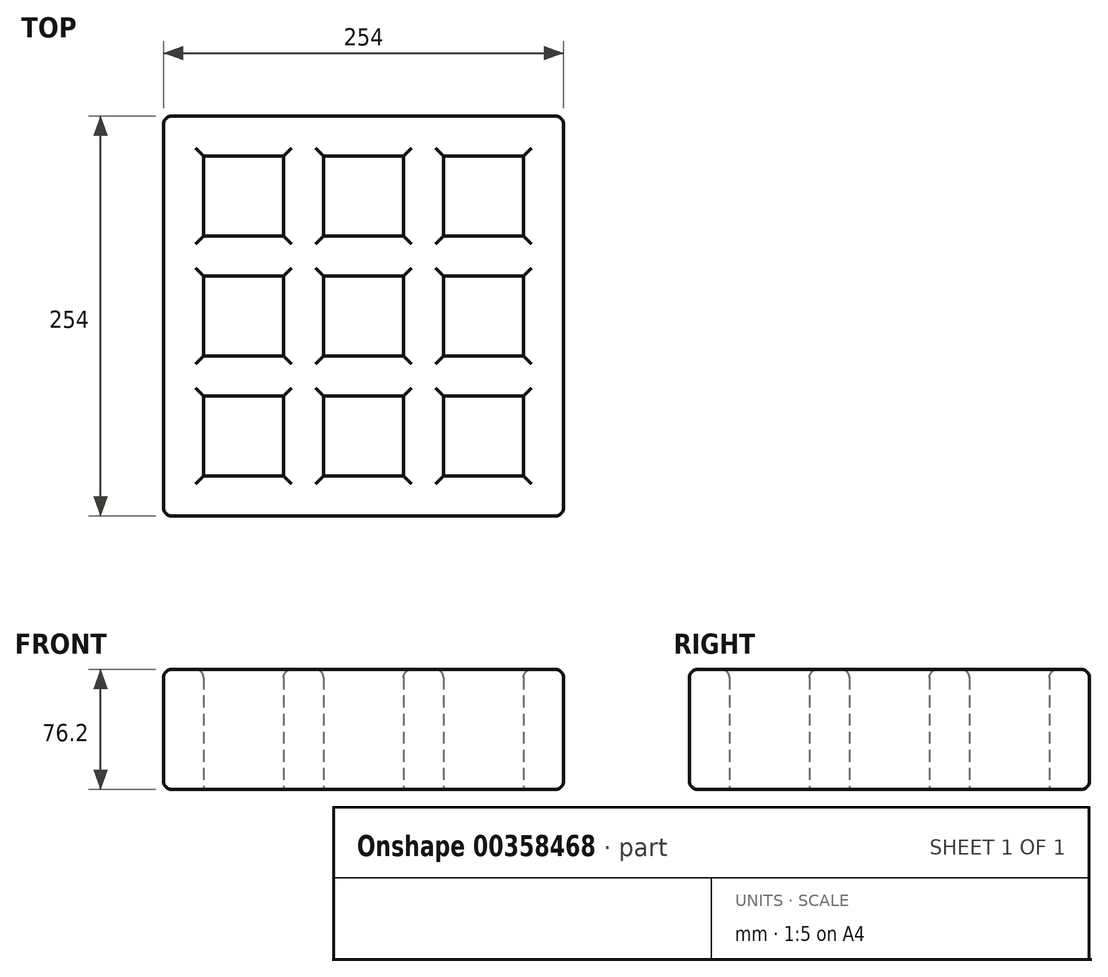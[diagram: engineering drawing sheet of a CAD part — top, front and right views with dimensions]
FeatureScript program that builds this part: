
annotation { "Feature Type Name" : "Feature", "Feature Type Description" : "" }
export const myFeature = defineFeature(function(context is Context, id is Id, definition is map)
    precondition{}
    {
        {
            var Q0;
            Q0=qCreatedBy(makeId("Top.planeOp"),FACE);
            var sketch = newSketch(context, id + "F0", { "sketchPlane" : qUnion([Q0])});
            skLineSegment(sketch, "E0.bottom", {"start": v(-126.07, 146.76) * mm, "end": v(127.93, 146.76) * mm});
            skLineSegment(sketch, "E0.top", {"start": v(-126.07, -107.24) * mm, "end": v(127.93, -107.24) * mm});
            skLineSegment(sketch, "E0.left", {"start": v(-126.07, 146.76) * mm, "end": v(-126.07, -107.24) * mm});
            skLineSegment(sketch, "E0.right", {"start": v(127.93, 146.76) * mm, "end": v(127.93, -107.24) * mm});
            skLineSegment(sketch, "E1.bottom", {"start": v(-100.67, 121.36) * mm, "end": v(-49.87, 121.36) * mm});
            skLineSegment(sketch, "E1.top", {"start": v(-100.67, 70.56) * mm, "end": v(-49.87, 70.56) * mm});
            skLineSegment(sketch, "E1.left", {"start": v(-100.67, 121.36) * mm, "end": v(-100.67, 70.56) * mm});
            skLineSegment(sketch, "E1.right", {"start": v(-49.87, 121.36) * mm, "end": v(-49.87, 70.56) * mm});
            skLineSegment(sketch, "E2.0.1.0", {"start": v(-49.87, 45.16) * mm, "end": v(-49.87, -5.64) * mm});
            skLineSegment(sketch, "E2.0.1.1", {"start": v(-100.67, 45.16) * mm, "end": v(-100.67, -5.64) * mm});
            skLineSegment(sketch, "E2.0.1.2", {"start": v(-100.67, -5.64) * mm, "end": v(-49.87, -5.64) * mm});
            skLineSegment(sketch, "E2.0.1.3", {"start": v(-100.67, 45.16) * mm, "end": v(-49.87, 45.16) * mm});
            skLineSegment(sketch, "E2.0.2.0", {"start": v(-49.87, -31.04) * mm, "end": v(-49.87, -81.84) * mm});
            skLineSegment(sketch, "E2.0.2.1", {"start": v(-100.67, -31.04) * mm, "end": v(-100.67, -81.84) * mm});
            skLineSegment(sketch, "E2.0.2.2", {"start": v(-100.67, -81.84) * mm, "end": v(-49.87, -81.84) * mm});
            skLineSegment(sketch, "E2.0.2.3", {"start": v(-100.67, -31.04) * mm, "end": v(-49.87, -31.04) * mm});
            skLineSegment(sketch, "E2.1.0.0", {"start": v(26.33, 121.36) * mm, "end": v(26.33, 70.56) * mm});
            skLineSegment(sketch, "E2.1.0.1", {"start": v(-24.47, 121.36) * mm, "end": v(-24.47, 70.56) * mm});
            skLineSegment(sketch, "E2.1.0.2", {"start": v(-24.47, 70.56) * mm, "end": v(26.33, 70.56) * mm});
            skLineSegment(sketch, "E2.1.0.3", {"start": v(-24.47, 121.36) * mm, "end": v(26.33, 121.36) * mm});
            skLineSegment(sketch, "E2.1.1.0", {"start": v(26.33, 45.16) * mm, "end": v(26.33, -5.64) * mm});
            skLineSegment(sketch, "E2.1.1.1", {"start": v(-24.47, 45.16) * mm, "end": v(-24.47, -5.64) * mm});
            skLineSegment(sketch, "E2.1.1.2", {"start": v(-24.47, -5.64) * mm, "end": v(26.33, -5.64) * mm});
            skLineSegment(sketch, "E2.1.1.3", {"start": v(-24.47, 45.16) * mm, "end": v(26.33, 45.16) * mm});
            skLineSegment(sketch, "E2.1.2.0", {"start": v(26.33, -31.04) * mm, "end": v(26.33, -81.84) * mm});
            skLineSegment(sketch, "E2.1.2.1", {"start": v(-24.47, -31.04) * mm, "end": v(-24.47, -81.84) * mm});
            skLineSegment(sketch, "E2.1.2.2", {"start": v(-24.47, -81.84) * mm, "end": v(26.33, -81.84) * mm});
            skLineSegment(sketch, "E2.1.2.3", {"start": v(-24.47, -31.04) * mm, "end": v(26.33, -31.04) * mm});
            skLineSegment(sketch, "E2.2.0.0", {"start": v(102.53, 121.36) * mm, "end": v(102.53, 70.56) * mm});
            skLineSegment(sketch, "E2.2.0.1", {"start": v(51.73, 121.36) * mm, "end": v(51.73, 70.56) * mm});
            skLineSegment(sketch, "E2.2.0.2", {"start": v(51.73, 70.56) * mm, "end": v(102.53, 70.56) * mm});
            skLineSegment(sketch, "E2.2.0.3", {"start": v(51.73, 121.36) * mm, "end": v(102.53, 121.36) * mm});
            skLineSegment(sketch, "E2.2.1.0", {"start": v(102.53, 45.16) * mm, "end": v(102.53, -5.64) * mm});
            skLineSegment(sketch, "E2.2.1.1", {"start": v(51.73, 45.16) * mm, "end": v(51.73, -5.64) * mm});
            skLineSegment(sketch, "E2.2.1.2", {"start": v(51.73, -5.64) * mm, "end": v(102.53, -5.64) * mm});
            skLineSegment(sketch, "E2.2.1.3", {"start": v(51.73, 45.16) * mm, "end": v(102.53, 45.16) * mm});
            skLineSegment(sketch, "E2.2.2.0", {"start": v(102.53, -31.04) * mm, "end": v(102.53, -81.84) * mm});
            skLineSegment(sketch, "E2.2.2.1", {"start": v(51.73, -31.04) * mm, "end": v(51.73, -81.84) * mm});
            skLineSegment(sketch, "E2.2.2.2", {"start": v(51.73, -81.84) * mm, "end": v(102.53, -81.84) * mm});
            skLineSegment(sketch, "E2.2.2.3", {"start": v(51.73, -31.04) * mm, "end": v(102.53, -31.04) * mm});
            skLineSegment(sketch, "E2.direction1", {"start": v(-100.67, 70.56) * mm, "end": v(-24.47, 70.56) * mm, "construction": true});
            skLineSegment(sketch, "E2.direction2", {"start": v(-100.67, 70.56) * mm, "end": v(-100.67, -5.64) * mm, "construction": true});
            skSolve(sketch);
        }
        {
            var Q0;
            Q0=makeQuery(id+"F0.imprint","IMPRINT",FACE,{"disambiguationData":[TD([[makeQuery(id+"F0.imprint","IMPRINT",EDGE,{"derivedFrom":sQuery(id+"F0.wireOp",EDGE,"E0.bottom")}),-1.0]])]});
            extrude(context, id + "F1", {"entities" : qUnion([Q0]), "depth" : 76.2 * mm});
        }
        {
            var Q0;
            Q0=makeQuery(id+"F1.opExtrude","CAP_EDGE",EDGE,{"disambiguationData":[OSD([sQuery(id+"F0.wireOp",EDGE,"E0.left")])],"isStart":false});
            var Q1;
            Q1=makeQuery(id+"F1.opExtrude","CAP_EDGE",EDGE,{"disambiguationData":[OSD([sQuery(id+"F0.wireOp",EDGE,"E0.top")])],"isStart":false});
            var Q2;
            Q2=makeQuery(id+"F1.opExtrude","SWEPT_EDGE",EDGE,{"disambiguationData":[OSD([sQuery(id+"F0.wireOp",EDGE,"E0.top"),sQuery(id+"F0.wireOp",EDGE,"E0.left")])]});
            var Q3;
            Q3=makeQuery(id+"F1.opExtrude","CAP_EDGE",EDGE,{"disambiguationData":[OSD([sQuery(id+"F0.wireOp",EDGE,"E0.top")])],"isStart":true});
            var Q4;
            Q4=makeQuery(id+"F1.opExtrude","CAP_EDGE",EDGE,{"disambiguationData":[OSD([sQuery(id+"F0.wireOp",EDGE,"E0.left")])],"isStart":true});
            var Q5;
            Q5=makeQuery(id+"F1.opExtrude","SWEPT_EDGE",EDGE,{"disambiguationData":[OSD([sQuery(id+"F0.wireOp",EDGE,"E0.bottom"),sQuery(id+"F0.wireOp",EDGE,"E0.left")])]});
            var Q6;
            Q6=makeQuery(id+"F1.opExtrude","CAP_FACE",FACE,{"disambiguationData":[OSD([sQuery(id+"F0.wireOp",EDGE,"E0.bottom"),sQuery(id+"F0.wireOp",EDGE,"E0.top"),sQuery(id+"F0.wireOp",EDGE,"E0.left"),sQuery(id+"F0.wireOp",EDGE,"E0.right"),sQuery(id+"F0.wireOp",EDGE,"E1.bottom"),sQuery(id+"F0.wireOp",EDGE,"E1.top"),sQuery(id+"F0.wireOp",EDGE,"E1.left"),sQuery(id+"F0.wireOp",EDGE,"E1.right"),sQuery(id+"F0.wireOp",EDGE,"E2.0.1.0"),sQuery(id+"F0.wireOp",EDGE,"E2.0.1.1"),sQuery(id+"F0.wireOp",EDGE,"E2.0.1.2"),sQuery(id+"F0.wireOp",EDGE,"E2.0.1.3"),sQuery(id+"F0.wireOp",EDGE,"E2.0.2.0"),sQuery(id+"F0.wireOp",EDGE,"E2.0.2.1"),sQuery(id+"F0.wireOp",EDGE,"E2.0.2.2"),sQuery(id+"F0.wireOp",EDGE,"E2.0.2.3"),sQuery(id+"F0.wireOp",EDGE,"E2.1.0.0"),sQuery(id+"F0.wireOp",EDGE,"E2.1.0.1"),sQuery(id+"F0.wireOp",EDGE,"E2.1.0.2"),sQuery(id+"F0.wireOp",EDGE,"E2.1.0.3"),sQuery(id+"F0.wireOp",EDGE,"E2.1.1.0"),sQuery(id+"F0.wireOp",EDGE,"E2.1.1.1"),sQuery(id+"F0.wireOp",EDGE,"E2.1.1.2"),sQuery(id+"F0.wireOp",EDGE,"E2.1.1.3"),sQuery(id+"F0.wireOp",EDGE,"E2.1.2.0"),sQuery(id+"F0.wireOp",EDGE,"E2.1.2.1"),sQuery(id+"F0.wireOp",EDGE,"E2.1.2.2"),sQuery(id+"F0.wireOp",EDGE,"E2.1.2.3"),sQuery(id+"F0.wireOp",EDGE,"E2.2.0.0"),sQuery(id+"F0.wireOp",EDGE,"E2.2.0.1"),sQuery(id+"F0.wireOp",EDGE,"E2.2.0.2"),sQuery(id+"F0.wireOp",EDGE,"E2.2.0.3"),sQuery(id+"F0.wireOp",EDGE,"E2.2.1.0"),sQuery(id+"F0.wireOp",EDGE,"E2.2.1.1"),sQuery(id+"F0.wireOp",EDGE,"E2.2.1.2"),sQuery(id+"F0.wireOp",EDGE,"E2.2.1.3"),sQuery(id+"F0.wireOp",EDGE,"E2.2.2.0"),sQuery(id+"F0.wireOp",EDGE,"E2.2.2.1"),sQuery(id+"F0.wireOp",EDGE,"E2.2.2.2"),sQuery(id+"F0.wireOp",EDGE,"E2.2.2.3")])],"isStart":false});
            var Q7;
            Q7=makeQuery(id+"F1.opExtrude","SWEPT_FACE",FACE,{"disambiguationData":[OSD([sQuery(id+"F0.wireOp",EDGE,"E0.right")])]});
            var Q8;
            Q8=makeQuery(id+"F1.opExtrude","CAP_EDGE",EDGE,{"disambiguationData":[OSD([sQuery(id+"F0.wireOp",EDGE,"E0.bottom")])],"isStart":true});
            fillet(context, id + "F2", {"entities" : qUnion([Q0, Q1, Q2, Q3, Q4, Q5, Q6, Q7, Q8]), "radius" : 5.08 * mm, "tangentPropagation" : true, "allowEdgeOverflow" : false});
        }
    });
